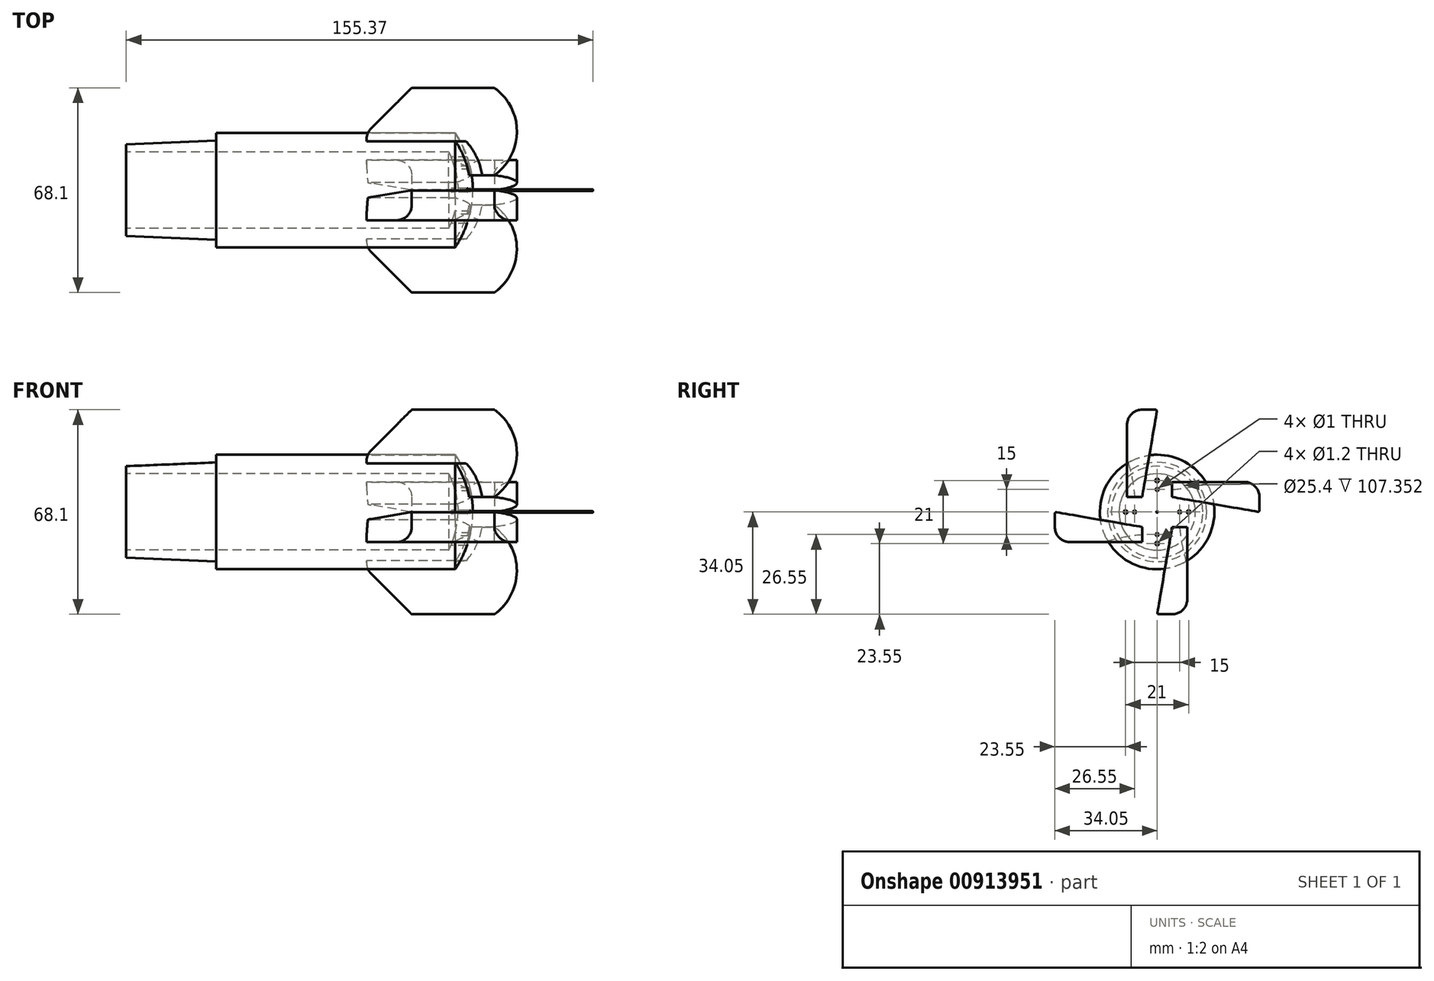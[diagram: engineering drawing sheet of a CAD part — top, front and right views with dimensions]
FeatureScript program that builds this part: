
annotation { "Feature Type Name" : "Feature", "Feature Type Description" : "" }
export const myFeature = defineFeature(function(context is Context, id is Id, definition is map)
    precondition{}
    {
        {
            var Q0;
            Q0=qCreatedBy(makeId("Front.planeOp"),FACE);
            var sketch = newSketch(context, id + "F0", { "sketchPlane" : qUnion([Q0])});
            skLineSegment(sketch, "E0", {"start": v(0, 0) * mm, "end": v(27.5, 0) * mm});
            skLineSegment(sketch, "E1", {"start": v(0, 0) * mm, "end": v(15, 15) * mm});
            skLineSegment(sketch, "E2", {"start": v(15, 15) * mm, "end": v(42.5, 15) * mm});
            skArc(sketch, "E3", {"start": v(34.07, -14.05) * mm, "mid": v(31.73, -6.58) * mm, "end": v(27.5, 0) * mm});
            skPoint(sketch, "E4.end.orphan", {"position": v(31.41, -14.05) * mm});
            skArc(sketch, "E5.trimOffspring", {"start": v(42.5, -14.05) * mm, "mid": v(50, 0.47) * mm, "end": v(42.5, 15) * mm});
            skLineSegment(sketch, "E6", {"start": v(34.07, -14.05) * mm, "end": v(42.5, -14.05) * mm});
            skSolve(sketch);
        }
        {
            var Q0;
            {var subQ1=sQuery(id+"F0.wireOp",EDGE,"E1");Q0=makeQuery(id+"F0.imprint","IMPRINT",FACE,{"disambiguationData":[TD([[makeQuery(id+"F0.imprint","IMPRINT",EDGE,{"derivedFrom":subQ1}),-1.0]])]});}
            extrude(context, id + "F1", {"entities" : qUnion([Q0]), "depth" : 10 * mm, "offsetDistance" : 25 * mm});
        }
        {
            var Q0;
            Q0=makeQuery(id+"F1.opExtrude","SWEPT_EDGE",EDGE,{"disambiguationData":[OSD([sQuery(id+"F0.wireOp",EDGE,"E5.trimOffspring"),sQuery(id+"F0.wireOp",EDGE,"E6")])]});
            cPlane(context, id + "F2", {"entities" : qUnion([Q0]), "cplaneType" : CPlaneType.LINE_ANGLE, "offset" : 25 * mm, "angle" : 90 * degree, "width" : 150 * mm, "height" : 150 * mm});
        }
        {
            var Q0;
            Q0=qCreatedBy(id+"F2.planeOp",FACE);
            var sketch = newSketch(context, id + "F3", { "sketchPlane" : qUnion([Q0])});
            skLineSegment(sketch, "E7", {"start": v(0, -75.7) * mm, "end": v(-5, -75.7) * mm});
            skLineSegment(sketch, "E8", {"start": v(0, -14.11) * mm, "end": v(-5, -14.11) * mm});
            skLineSegment(sketch, "E9", {"start": v(0, -14.11) * mm, "end": v(0, 14.94) * mm});
            skLineSegment(sketch, "E10", {"start": v(0, 14.94) * mm, "end": v(-5, -14.11) * mm});
            skSolve(sketch);
        }
        {
            var Q0;
            Q0=makeQuery(id+"F3.imprint","IMPRINT",FACE,{"disambiguationData":[TD([[makeQuery(id+"F3.imprint","IMPRINT",EDGE,{"derivedFrom":sQuery(id+"F3.wireOp",EDGE,"E8")}),-1.0]])]});
            extrude(context, id + "F4", {"entities" : qUnion([Q0]), "operationType" : NewBodyOperationType.REMOVE, "endBound" : BoundingType.THROUGH_ALL, "depth" : 25 * mm, "offsetDistance" : 25 * mm, "hasSecondDirection" : true, "secondDirectionOppositeDirection" : true, "secondDirectionDepth" : 65.4 * mm});
        }
        {
            var Q0;
            Q0=makeQuery(id+"F1.opExtrude","CAP_EDGE",EDGE,{"disambiguationData":[OSD([sQuery(id+"F0.wireOp",EDGE,"E2")])],"isStart":false});
            fillet(context, id + "F5", {"entities" : qUnion([Q0]), "radius" : 5 * mm, "tangentPropagation" : true, "allowEdgeOverflow" : false});
        }
        {
            var Q0;
            Q0=makeQuery(id+"F1.opExtrude","CAP_EDGE",EDGE,{"disambiguationData":[OSD([sQuery(id+"F0.wireOp",EDGE,"E2")])],"isStart":true});
            fillet(context, id + "F6", {"entities" : qUnion([Q0]), "radius" : 1 * mm, "tangentPropagation" : true, "allowEdgeOverflow" : false});
        }
        {
            var Q0;
            Q0=makeQuery(id+"F6.opFillet","BLEND_EDGE",EDGE,{"blendedFrom":[makeQuery(id+"F1.opExtrude","CAP_EDGE",EDGE,{"disambiguationData":[OSD([sQuery(id+"F0.wireOp",EDGE,"E2")])],"isStart":true}),makeQuery(id+"F4.boolean.opBoolean","COPY",FACE,{"derivedFrom":makeQuery(id+"F4.opExtrude","SWEPT_FACE",FACE,{"disambiguationData":[OSD([sQuery(id+"F3.wireOp",EDGE,"E10")])]})})],"blendedInto":[makeQuery(id+"F4.boolean.opBoolean","COPY",FACE,{"derivedFrom":makeQuery(id+"F4.opExtrude","SWEPT_FACE",FACE,{"disambiguationData":[OSD([sQuery(id+"F3.wireOp",EDGE,"E10")])]})})]});
            fillet(context, id + "F7", {"entities" : qUnion([Q0]), "radius" : 0.5 * mm, "tangentPropagation" : true, "allowEdgeOverflow" : false});
        }
        {
            var Q0;
            Q0=qCreatedBy(makeId("Front.planeOp"),FACE);
            var sketch = newSketch(context, id + "F8", { "sketchPlane" : qUnion([Q0])});
            skLineSegment(sketch, "E11", {"start": v(0, 0) * mm, "end": v(29.48, 0) * mm});
            skLineSegment(sketch, "E12", {"start": v(0, 0) * mm, "end": v(-50, 0) * mm});
            skLineSegment(sketch, "E13", {"start": v(-50, 0) * mm, "end": v(-50, -2.54) * mm});
            skLineSegment(sketch, "E14", {"start": v(30.37, -19.05) * mm, "end": v(35.37, -19.05) * mm});
            skLineSegment(sketch, "E15", {"start": v(-80, -6.35) * mm, "end": v(-80, -3.81) * mm});
            skLineSegment(sketch, "E16", {"start": v(-80, -3.81) * mm, "end": v(-50, -2.54) * mm});
            skLineSegment(sketch, "E17", {"start": v(-48.68, -6.35) * mm, "end": v(-80, -6.35) * mm});
            skLineSegment(sketch, "E18", {"start": v(-48.68, -6.35) * mm, "end": v(27.35, -6.35) * mm});
            skArc(sketch, "E19.trimOffspring", {"start": v(35.37, -19.05) * mm, "mid": v(33.8, -9.1) * mm, "end": v(29.48, 0) * mm});
            skArc(sketch, "E20.trimOffspring", {"start": v(30.37, -19.05) * mm, "mid": v(29.55, -12.54) * mm, "end": v(27.35, -6.35) * mm});
            skLineSegment(sketch, "E21", {"start": v(35.37, -19.05) * mm, "end": v(75.37, -19.05) * mm});
            skLineSegment(sketch, "E22", {"start": v(75.37, -19.05) * mm, "end": v(75.37, -19.05) * mm});
            skLineSegment(sketch, "E23", {"start": v(75.12, -18.8) * mm, "end": v(35.37, -18.8) * mm});
            skPoint(sketch, "E24.visualSharp", {"position": v(75.37, -18.8) * mm});
            skArc(sketch, "E24.filletArc", {"start": v(75.37, -19.05) * mm, "mid": v(75.3, -18.87) * mm, "end": v(75.12, -18.8) * mm});
            skSolve(sketch);
        }
        {
            var Q0;
            Q0=qCreatedBy(makeId("Right.planeOp"),FACE);
            var sketch = newSketch(context, id + "F9", { "sketchPlane" : qUnion([Q0])});
            skLineSegment(sketch, "E25", {"start": v(0, 0) * mm, "end": v(0, -19.05) * mm});
            skCircle(sketch, "E26", {"center": v(0, -19.05) * mm, "radius": 19.05 * mm});
            skSolve(sketch);
        }
        {
            var Q0;
            Q0=makeQuery(id+"F1.opExtrude","SWEPT_BODY",BODY,{"disambiguationData":[OSD([sQuery(id+"F0.wireOp",EDGE,"E0"),sQuery(id+"F0.wireOp",EDGE,"E1"),sQuery(id+"F0.wireOp",EDGE,"E2"),sQuery(id+"F0.wireOp",EDGE,"E3"),sQuery(id+"F0.wireOp",EDGE,"E5.trimOffspring"),sQuery(id+"F0.wireOp",EDGE,"E6")])]});
            var Q1;
            Q1=sQuery(id+"F9.wireOp",EDGE,"E26");
            circularPattern(context, id + "F10", {"entities" : qUnion([Q0]), "axis" : qUnion([Q1]), "angle" : 360 * degree, "instanceCount" : 4, "equalSpace" : true});
        }
        {
            var Q0;
            Q0=makeQuery(id+"F8.imprint","IMPRINT",FACE,{"disambiguationData":[TD([[makeQuery(id+"F8.imprint","IMPRINT",EDGE,{"derivedFrom":sQuery(id+"F8.wireOp",EDGE,"E11")}),-1.0]])]});
            var Q1;
            {var subQ0=sQuery(id+"F8.wireOp",EDGE,"E21");Q1=makeQuery(id+"F8.imprint","IMPRINT",FACE,{"disambiguationData":[TD([[makeQuery(id+"F8.imprint","IMPRINT",EDGE,{"derivedFrom":subQ0}),1.0]])]});}
            var Q2;
            Q2=sQuery(id+"F9.wireOp",EDGE,"E26");
            revolve(context, id + "F11", {"surfaceOperationType" : NewSurfaceOperationType.NEW, "entities" : qUnion([Q0, Q1]), "axis" : qUnion([Q2]), "revolveType" : RevolveType.FULL});
        }
        {
            var Q0;
            Q0=makeQuery(id+"F1.opExtrude","SWEPT_FACE",FACE,{"disambiguationData":[OSD([sQuery(id+"F0.wireOp",EDGE,"E0")])]});
            var Q1;
            Q1=makeQuery(id+"F11.opRevolve","SWEPT_FACE",FACE,{"disambiguationData":[OSD([sQuery(id+"F8.wireOp",EDGE,"E11"),sQuery(id+"F8.wireOp",EDGE,"E12")])]});
            extrude(context, id + "F12", {"entities" : qUnion([Q0]), "endBound" : BoundingType.UP_TO_SURFACE, "depth" : 25 * mm, "endBoundEntityFace" : qUnion([Q1]), "offsetDistance" : 25 * mm});
        }
        {
            var Q0;
            Q0=makeQuery(id+"F10.opPattern","COPY",FACE,{"derivedFrom":makeQuery(id+"F1.opExtrude","SWEPT_FACE",FACE,{"disambiguationData":[OSD([sQuery(id+"F0.wireOp",EDGE,"E0")])]}),"instanceName":"1"});
            var Q1;
            Q1=makeQuery(id+"F11.opRevolve","SWEPT_FACE",FACE,{"disambiguationData":[OSD([sQuery(id+"F8.wireOp",EDGE,"E11"),sQuery(id+"F8.wireOp",EDGE,"E12")])]});
            extrude(context, id + "F13", {"entities" : qUnion([Q0]), "endBound" : BoundingType.UP_TO_SURFACE, "depth" : 25 * mm, "endBoundEntityFace" : qUnion([Q1]), "offsetDistance" : 25 * mm});
        }
        {
            var Q0;
            Q0=makeQuery(id+"F10.opPattern","COPY",FACE,{"derivedFrom":makeQuery(id+"F1.opExtrude","SWEPT_FACE",FACE,{"disambiguationData":[OSD([sQuery(id+"F0.wireOp",EDGE,"E0")])]}),"instanceName":"2"});
            var Q1;
            Q1=makeQuery(id+"F11.opRevolve","SWEPT_FACE",FACE,{"disambiguationData":[OSD([sQuery(id+"F8.wireOp",EDGE,"E11"),sQuery(id+"F8.wireOp",EDGE,"E12")])]});
            extrude(context, id + "F14", {"entities" : qUnion([Q0]), "endBound" : BoundingType.UP_TO_SURFACE, "depth" : 25 * mm, "endBoundEntityFace" : qUnion([Q1]), "offsetDistance" : 25 * mm});
        }
        {
            var Q0;
            Q0=makeQuery(id+"F10.opPattern","COPY",FACE,{"derivedFrom":makeQuery(id+"F1.opExtrude","SWEPT_FACE",FACE,{"disambiguationData":[OSD([sQuery(id+"F0.wireOp",EDGE,"E0")])]}),"instanceName":"3"});
            var Q1;
            Q1=makeQuery(id+"F11.opRevolve","SWEPT_FACE",FACE,{"disambiguationData":[OSD([sQuery(id+"F8.wireOp",EDGE,"E11"),sQuery(id+"F8.wireOp",EDGE,"E12")])]});
            extrude(context, id + "F15", {"entities" : qUnion([Q0]), "endBound" : BoundingType.UP_TO_SURFACE, "depth" : 25 * mm, "endBoundEntityFace" : qUnion([Q1]), "offsetDistance" : 25 * mm});
        }
        {
            var Q0;
            Q0=makeQuery(id+"F15.opExtrude","SWEPT_FACE",FACE,{"disambiguationData":[OSD([sQuery(id+"F0.wireOp",EDGE,"E0"),sQuery(id+"F0.wireOp",EDGE,"E3")])]});
            var Q1;
            Q1=makeQuery(id+"F10.opPattern","COPY",FACE,{"derivedFrom":makeQuery(id+"F1.opExtrude","SWEPT_FACE",FACE,{"disambiguationData":[OSD([sQuery(id+"F0.wireOp",EDGE,"E3")])]}),"instanceName":"3"});
            extrude(context, id + "F16", {"entities" : qUnion([Q0]), "endBound" : BoundingType.UP_TO_SURFACE, "depth" : 5 * mm, "endBoundEntityFace" : qUnion([Q1]), "offsetDistance" : 25 * mm});
        }
        {
            var Q0;
            Q0=makeQuery(id+"F12.opExtrude","SWEPT_FACE",FACE,{"disambiguationData":[OSD([sQuery(id+"F0.wireOp",EDGE,"E0"),sQuery(id+"F0.wireOp",EDGE,"E3")])]});
            var Q1;
            Q1=makeQuery(id+"F1.opExtrude","SWEPT_FACE",FACE,{"disambiguationData":[OSD([sQuery(id+"F0.wireOp",EDGE,"E3")])]});
            extrude(context, id + "F17", {"entities" : qUnion([Q0]), "endBound" : BoundingType.UP_TO_SURFACE, "depth" : 25 * mm, "endBoundEntityFace" : qUnion([Q1]), "offsetDistance" : 25 * mm});
        }
        {
            var Q0;
            Q0=makeQuery(id+"F13.opExtrude","SWEPT_FACE",FACE,{"disambiguationData":[OSD([sQuery(id+"F0.wireOp",EDGE,"E0"),sQuery(id+"F0.wireOp",EDGE,"E3")])]});
            var Q1;
            Q1=makeQuery(id+"F10.opPattern","COPY",FACE,{"derivedFrom":makeQuery(id+"F1.opExtrude","SWEPT_FACE",FACE,{"disambiguationData":[OSD([sQuery(id+"F0.wireOp",EDGE,"E3")])]}),"instanceName":"1"});
            extrude(context, id + "F18", {"entities" : qUnion([Q0]), "endBound" : BoundingType.UP_TO_SURFACE, "depth" : 25 * mm, "endBoundEntityFace" : qUnion([Q1]), "offsetDistance" : 25 * mm});
        }
        {
            var Q0;
            Q0=makeQuery(id+"F14.opExtrude","SWEPT_FACE",FACE,{"disambiguationData":[OSD([sQuery(id+"F0.wireOp",EDGE,"E0"),sQuery(id+"F0.wireOp",EDGE,"E3")])]});
            var Q1;
            Q1=makeQuery(id+"F10.opPattern","COPY",FACE,{"derivedFrom":makeQuery(id+"F1.opExtrude","SWEPT_FACE",FACE,{"disambiguationData":[OSD([sQuery(id+"F0.wireOp",EDGE,"E3")])]}),"instanceName":"2"});
            extrude(context, id + "F19", {"entities" : qUnion([Q0]), "endBound" : BoundingType.UP_TO_SURFACE, "depth" : 25 * mm, "endBoundEntityFace" : qUnion([Q1]), "offsetDistance" : 25 * mm});
        }
        {
            var Q0;
            Q0=makeQuery(id+"F1.opExtrude","SWEPT_BODY",BODY,{"disambiguationData":[OSD([sQuery(id+"F0.wireOp",EDGE,"E0"),sQuery(id+"F0.wireOp",EDGE,"E1"),sQuery(id+"F0.wireOp",EDGE,"E2"),sQuery(id+"F0.wireOp",EDGE,"E3"),sQuery(id+"F0.wireOp",EDGE,"E5.trimOffspring"),sQuery(id+"F0.wireOp",EDGE,"E6")])]});
            var Q1;
            Q1=makeQuery(id+"F10.opPattern","COPY",BODY,{"derivedFrom":makeQuery(id+"F1.opExtrude","SWEPT_BODY",BODY,{"disambiguationData":[OSD([sQuery(id+"F0.wireOp",EDGE,"E0"),sQuery(id+"F0.wireOp",EDGE,"E1"),sQuery(id+"F0.wireOp",EDGE,"E2"),sQuery(id+"F0.wireOp",EDGE,"E3"),sQuery(id+"F0.wireOp",EDGE,"E5.trimOffspring"),sQuery(id+"F0.wireOp",EDGE,"E6")])]}),"instanceName":"1"});
            var Q2;
            Q2=makeQuery(id+"F12.opExtrude","SWEPT_BODY",BODY,{"disambiguationData":[OSD([sQuery(id+"F0.wireOp",EDGE,"E0")])]});
            var Q3;
            Q3=makeQuery(id+"F13.opExtrude","SWEPT_BODY",BODY,{"disambiguationData":[OSD([sQuery(id+"F0.wireOp",EDGE,"E0")])]});
            var Q4;
            Q4=makeQuery(id+"F17.opExtrude","SWEPT_BODY",BODY,{"disambiguationData":[OSD([sQuery(id+"F0.wireOp",EDGE,"E0"),sQuery(id+"F0.wireOp",EDGE,"E3")])]});
            var Q5;
            Q5=makeQuery(id+"F11.opRevolve","SWEPT_BODY",BODY,{"disambiguationData":[OSD([sQuery(id+"F8.wireOp",EDGE,"E11"),sQuery(id+"F8.wireOp",EDGE,"E12"),sQuery(id+"F8.wireOp",EDGE,"E13"),sQuery(id+"F8.wireOp",EDGE,"E14"),sQuery(id+"F8.wireOp",EDGE,"E15"),sQuery(id+"F8.wireOp",EDGE,"E16"),sQuery(id+"F8.wireOp",EDGE,"E17"),sQuery(id+"F8.wireOp",EDGE,"E18"),sQuery(id+"F8.wireOp",EDGE,"E19.trimOffspring"),sQuery(id+"F8.wireOp",EDGE,"E20.trimOffspring")])]});
            var Q6;
            Q6=makeQuery(id+"F10.opPattern","COPY",BODY,{"derivedFrom":makeQuery(id+"F1.opExtrude","SWEPT_BODY",BODY,{"disambiguationData":[OSD([sQuery(id+"F0.wireOp",EDGE,"E0"),sQuery(id+"F0.wireOp",EDGE,"E1"),sQuery(id+"F0.wireOp",EDGE,"E2"),sQuery(id+"F0.wireOp",EDGE,"E3"),sQuery(id+"F0.wireOp",EDGE,"E5.trimOffspring"),sQuery(id+"F0.wireOp",EDGE,"E6")])]}),"instanceName":"3"});
            var Q7;
            Q7=makeQuery(id+"F10.opPattern","COPY",BODY,{"derivedFrom":makeQuery(id+"F1.opExtrude","SWEPT_BODY",BODY,{"disambiguationData":[OSD([sQuery(id+"F0.wireOp",EDGE,"E0"),sQuery(id+"F0.wireOp",EDGE,"E1"),sQuery(id+"F0.wireOp",EDGE,"E2"),sQuery(id+"F0.wireOp",EDGE,"E3"),sQuery(id+"F0.wireOp",EDGE,"E5.trimOffspring"),sQuery(id+"F0.wireOp",EDGE,"E6")])]}),"instanceName":"2"});
            var Q8;
            Q8=makeQuery(id+"F14.opExtrude","SWEPT_BODY",BODY,{"disambiguationData":[OSD([sQuery(id+"F0.wireOp",EDGE,"E0")])]});
            var Q9;
            Q9=makeQuery(id+"F18.opExtrude","SWEPT_BODY",BODY,{"disambiguationData":[OSD([sQuery(id+"F0.wireOp",EDGE,"E0"),sQuery(id+"F0.wireOp",EDGE,"E3")])]});
            var Q10;
            Q10=makeQuery(id+"F19.opExtrude","SWEPT_BODY",BODY,{"disambiguationData":[OSD([sQuery(id+"F0.wireOp",EDGE,"E0"),sQuery(id+"F0.wireOp",EDGE,"E3")])]});
            var Q11;
            Q11=makeQuery(id+"F15.opExtrude","SWEPT_BODY",BODY,{"disambiguationData":[OSD([sQuery(id+"F0.wireOp",EDGE,"E0")])]});
            var Q12;
            Q12=makeQuery(id+"F16.opExtrude","SWEPT_BODY",BODY,{"disambiguationData":[OSD([sQuery(id+"F0.wireOp",EDGE,"E0"),sQuery(id+"F0.wireOp",EDGE,"E3")])]});
            booleanBodies(context, id + "F20", {"operationType" : BooleanOperationType.UNION, "tools" : qUnion([Q0, Q1, Q2, Q3, Q4, Q5, Q6, Q7, Q8, Q9, Q10, Q11, Q12])});
        }
        {
            var Q0;
            Q0=makeQuery(id+"F10.opPattern","COPY",EDGE,{"derivedFrom":makeQuery(id+"F1.opExtrude","CAP_EDGE",EDGE,{"disambiguationData":[OSD([sQuery(id+"F0.wireOp",EDGE,"E3")])],"isStart":false}),"instanceName":"2"});
            fillet(context, id + "F21", {"entities" : qUnion([Q0]), "radius" : 5 * mm, "tangentPropagation" : true, "allowEdgeOverflow" : false});
        }
        {
            var Q0;
            Q0=makeQuery(id+"F10.opPattern","COPY",EDGE,{"derivedFrom":makeQuery(id+"F1.opExtrude","CAP_EDGE",EDGE,{"disambiguationData":[OSD([sQuery(id+"F0.wireOp",EDGE,"E3")])],"isStart":false}),"instanceName":"3"});
            var Q1;
            Q1=makeQuery(id+"F1.opExtrude","CAP_EDGE",EDGE,{"disambiguationData":[OSD([sQuery(id+"F0.wireOp",EDGE,"E3")])],"isStart":false});
            var Q2;
            Q2=makeQuery(id+"F10.opPattern","COPY",EDGE,{"derivedFrom":makeQuery(id+"F1.opExtrude","CAP_EDGE",EDGE,{"disambiguationData":[OSD([sQuery(id+"F0.wireOp",EDGE,"E3")])],"isStart":false}),"instanceName":"1"});
            fillet(context, id + "F22", {"entities" : qUnion([Q0, Q1, Q2]), "radius" : 5 * mm, "tangentPropagation" : true, "allowEdgeOverflow" : false});
        }
        {
            var Q0;
            {var subQ0=sQuery(id+"F0.wireOp",EDGE,"E1");var subQ1=sQuery(id+"F0.wireOp",EDGE,"E0");Q0=makeQuery(id+"F20.opBoolean","MERGE",EDGE,{"derivedFrom":[makeQuery(id+"F10.opPattern","COPY",EDGE,{"derivedFrom":makeQuery(id+"F1.opExtrude","SWEPT_EDGE",EDGE,{"disambiguationData":[OSD([subQ1,subQ0])]}),"instanceName":"2"}),makeQuery(id+"F14.opExtrude","CAP_EDGE",EDGE,{"disambiguationData":[OSD([subQ1,subQ0])],"isStart":true})]});}
            fillet(context, id + "F23", {"entities" : qUnion([Q0]), "radius" : 5 * mm, "tangentPropagation" : true, "allowEdgeOverflow" : false});
        }
        {
            var Q0;
            {var subQ0=sQuery(id+"F0.wireOp",EDGE,"E1");var subQ1=sQuery(id+"F0.wireOp",EDGE,"E0");Q0=makeQuery(id+"F20.opBoolean","MERGE",EDGE,{"derivedFrom":[makeQuery(id+"F10.opPattern","COPY",EDGE,{"derivedFrom":makeQuery(id+"F1.opExtrude","SWEPT_EDGE",EDGE,{"disambiguationData":[OSD([subQ1,subQ0])]}),"instanceName":"3"}),makeQuery(id+"F15.opExtrude","CAP_EDGE",EDGE,{"disambiguationData":[OSD([subQ1,subQ0])],"isStart":true})]});}
            var Q1;
            {var subQ0=sQuery(id+"F0.wireOp",EDGE,"E1");var subQ1=sQuery(id+"F0.wireOp",EDGE,"E0");Q1=makeQuery(id+"F20.opBoolean","MERGE",EDGE,{"derivedFrom":[makeQuery(id+"F1.opExtrude","SWEPT_EDGE",EDGE,{"disambiguationData":[OSD([subQ1,subQ0])]}),makeQuery(id+"F12.opExtrude","CAP_EDGE",EDGE,{"disambiguationData":[OSD([subQ1,subQ0])],"isStart":true})]});}
            var Q2;
            {var subQ0=sQuery(id+"F0.wireOp",EDGE,"E1");var subQ1=sQuery(id+"F0.wireOp",EDGE,"E0");Q2=makeQuery(id+"F20.opBoolean","MERGE",EDGE,{"derivedFrom":[makeQuery(id+"F10.opPattern","COPY",EDGE,{"derivedFrom":makeQuery(id+"F1.opExtrude","SWEPT_EDGE",EDGE,{"disambiguationData":[OSD([subQ1,subQ0])]}),"instanceName":"1"}),makeQuery(id+"F13.opExtrude","CAP_EDGE",EDGE,{"disambiguationData":[OSD([subQ1,subQ0])],"isStart":true})]});}
            fillet(context, id + "F24", {"entities" : qUnion([Q0, Q1, Q2]), "radius" : 5 * mm, "tangentPropagation" : true, "allowEdgeOverflow" : false});
        }
        {
            var Q0;
            Q0=makeQuery(id+"F11.opRevolve","SWEPT_FACE",FACE,{"disambiguationData":[OSD([sQuery(id+"F8.wireOp",EDGE,"E13")])]});
            cPlane(context, id + "F25", {"entities" : qUnion([Q0]), "cplaneType" : CPlaneType.OFFSET, "offset" : 38.3 * mm, "width" : 150 * mm, "height" : 150 * mm});
        }
        {
            var Q0;
            Q0=qCreatedBy(id+"F25.planeOp",FACE);
            var sketch = newSketch(context, id + "F26", { "sketchPlane" : qUnion([Q0])});
            skPoint(sketch, "E27.MirrorCS.start.orphan", {"position": v(0, -19.05) * mm});
            skPoint(sketch, "E28.trimOffspring.end.orphan", {"position": v(18.25, -0.8) * mm});
            skPoint(sketch, "E29.trimOffspring.end.orphan", {"position": v(-18.25, -0.8) * mm});
            skPoint(sketch, "E30.trimOffspring.end.orphan", {"position": v(18.25, -37.3) * mm});
            skPoint(sketch, "E31.trimOffspring.end.orphan", {"position": v(-18.25, -37.3) * mm});
            skCircle(sketch, "E32", {"center": v(7.5, -19.05) * mm, "radius": 0.5 * mm});
            skCircle(sketch, "E33.MirrorC", {"center": v(-7.5, -19.05) * mm, "radius": 0.5 * mm});
            skCircle(sketch, "E34", {"center": v(0, -11.55) * mm, "radius": 0.5 * mm});
            skCircle(sketch, "E35.MirrorC", {"center": v(0, -26.55) * mm, "radius": 0.5 * mm});
            skCircle(sketch, "E36", {"center": v(0, -8.55) * mm, "radius": 0.6 * mm});
            skCircle(sketch, "E37.MirrorC", {"center": v(0, -29.55) * mm, "radius": 0.6 * mm});
            skCircle(sketch, "E38", {"center": v(10.5, -19.05) * mm, "radius": 0.6 * mm});
            skCircle(sketch, "E39.MirrorC", {"center": v(-10.5, -19.05) * mm, "radius": 0.6 * mm});
            skLineSegment(sketch, "E40", {"start": v(7.5, -19.05) * mm, "end": v(10.5, -19.05) * mm});
            skSolve(sketch);
        }
        {
            var Q0;
            Q0 = qSketchRegion(id + "F26", true);
            extrude(context, id + "F27", {"entities" : qUnion([Q0]), "operationType" : NewBodyOperationType.REMOVE, "oppositeDirection" : true, "depth" : 500 * mm, "offsetDistance" : 25 * mm});
        }
    });
